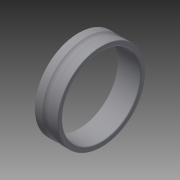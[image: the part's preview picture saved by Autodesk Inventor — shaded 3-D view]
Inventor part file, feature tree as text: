
AUTODESK INVENTOR PART (.ipt)
format: ipt  version: 2014 SP2 (Build 180246200, 246)  size: 159,744 bytes
history: native  units: mm
features: other x14, revolve x1, sketch x1
ambient origin geometry x8: Origin, YZ Plane, XZ Plane, XY Plane, X Axis, Y Axis, Z Axis, Center Point
bodies: Solid1 (feature_tree)
feature tree (16):
  revolve  "Revolution1"  [1 undecoded]
  other  "1_XY"
  other  "1_YZ"
  other  "1_ZX"
  other  "1_X"
  other  "1_Y"
  other  "1_Z"
  other  "1_Center"
  other  "1_Dummy_XY"
  other  "1_Dummy_YZ"
  other  "1_Dummy_ZX"
  other  "1_Dummy_X"
  other  "1_Dummy_Y"
  other  "1_Dummy_Z"
  other  "1_Dummy_Center"
  sketch  "Sketch_1"  dims[d0=360.0deg d1=0.0mm]
note: 1 required parameter value undecoded (feature->parameter linkage not recoverable at this tier; creation-order binding heuristic only, values carry confidence <= 0.55)
